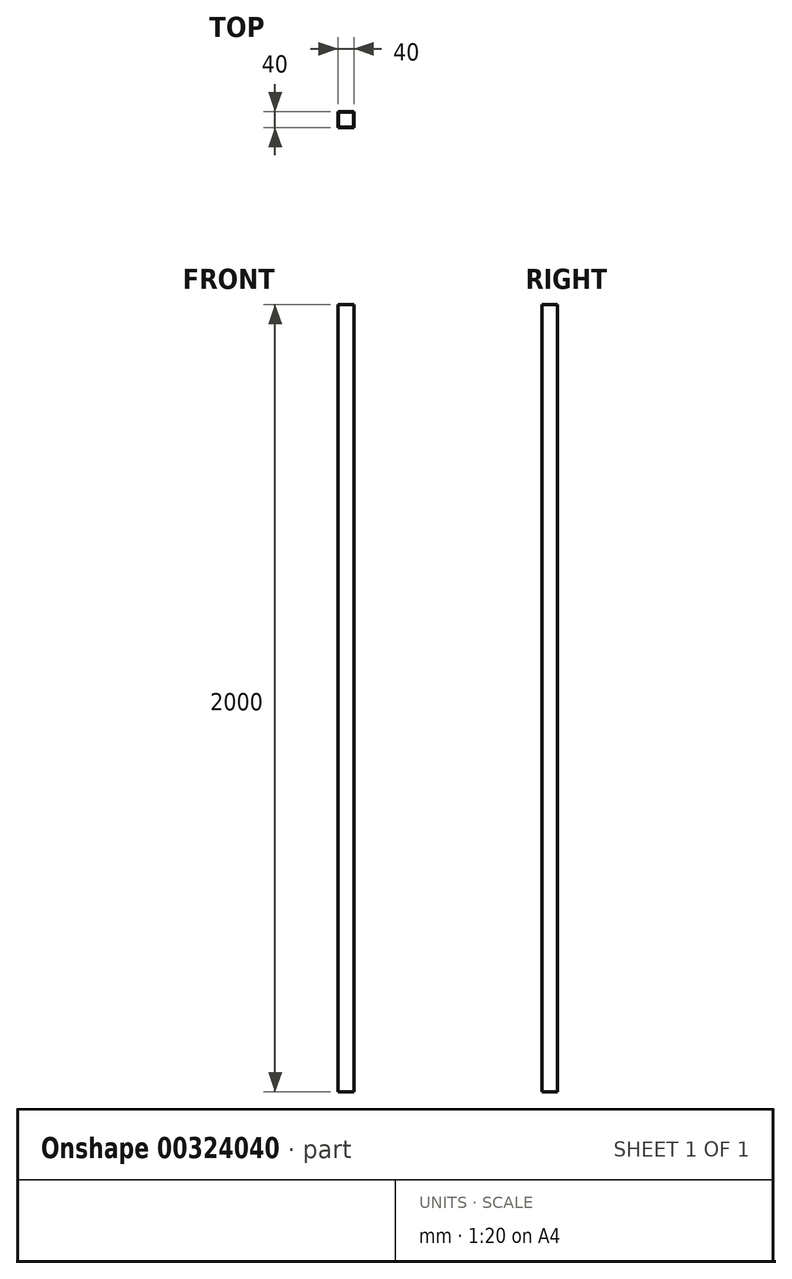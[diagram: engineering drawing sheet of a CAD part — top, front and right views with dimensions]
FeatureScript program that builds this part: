
annotation { "Feature Type Name" : "Feature", "Feature Type Description" : "" }
export const myFeature = defineFeature(function(context is Context, id is Id, definition is map)
    precondition{}
    {
        {
            var Q0;
            Q0=qCreatedBy(makeId("Top.planeOp"),FACE);
            var sketch = newSketch(context, id + "F0", { "sketchPlane" : qUnion([Q0])});
            skLineSegment(sketch, "E0.bottom", {"start": v(20, 20) * mm, "end": v(-20, 20) * mm});
            skLineSegment(sketch, "E0.top", {"start": v(20, -20) * mm, "end": v(-20, -20) * mm});
            skLineSegment(sketch, "E0.left", {"start": v(20, 20) * mm, "end": v(20, -20) * mm});
            skLineSegment(sketch, "E0.right", {"start": v(-20, 20) * mm, "end": v(-20, -20) * mm});
            skPoint(sketch, "E0.middle", {"position": v(0, 0) * mm});
            skSolve(sketch);
        }
        {
            var Q0;
            Q0=qCreatedBy(makeId("Top.planeOp"),FACE);
            var sketch = newSketch(context, id + "F1", { "sketchPlane" : qUnion([Q0])});
            skLineSegment(sketch, "E1.0", {"start": v(18.5, 18.5) * mm, "end": v(18.5, -18.5) * mm});
            skLineSegment(sketch, "E1.1", {"start": v(18.5, 18.5) * mm, "end": v(-18.5, 18.5) * mm});
            skLineSegment(sketch, "E1.2", {"start": v(-18.5, 18.5) * mm, "end": v(-18.5, -18.5) * mm});
            skLineSegment(sketch, "E1.3", {"start": v(18.5, -18.5) * mm, "end": v(-18.5, -18.5) * mm});
            skSolve(sketch);
        }
        {
            var Q0;
            Q0=makeQuery(id+"F0.imprint","IMPRINT",FACE,{"disambiguationData":[TD([[makeQuery(id+"F0.imprint","IMPRINT",EDGE,{"derivedFrom":sQuery(id+"F0.wireOp",EDGE,"E0.bottom")}),1.0]])]});
            var Q1;
            Q1=sQuery(id+"F0.wireOp",EDGE,"E0.bottom");
            var Q2;
            Q2=sQuery(id+"F1.wireOp",EDGE,"E1.0");
            var Q3;
            Q3=sQuery(id+"F0.wireOp",EDGE,"E0.left");
            var Q4;
            Q4=sQuery(id+"F1.wireOp",EDGE,"E1.1");
            var Q5;
            Q5=sQuery(id+"F1.wireOp",EDGE,"E1.2");
            var Q6;
            Q6=sQuery(id+"F0.wireOp",EDGE,"E0.right");
            var Q7;
            Q7=sQuery(id+"F1.wireOp",EDGE,"E1.3");
            var Q8;
            Q8=sQuery(id+"F0.wireOp",EDGE,"E0.top");
            extrude(context, id + "F2", {"entities" : qUnion([Q0]), "bodyType" : ToolBodyType.SURFACE, "surfaceEntities" : qUnion([Q1, Q2, Q3, Q4, Q5, Q6, Q7, Q8]), "depth" : 2000 * mm});
        }
    });
